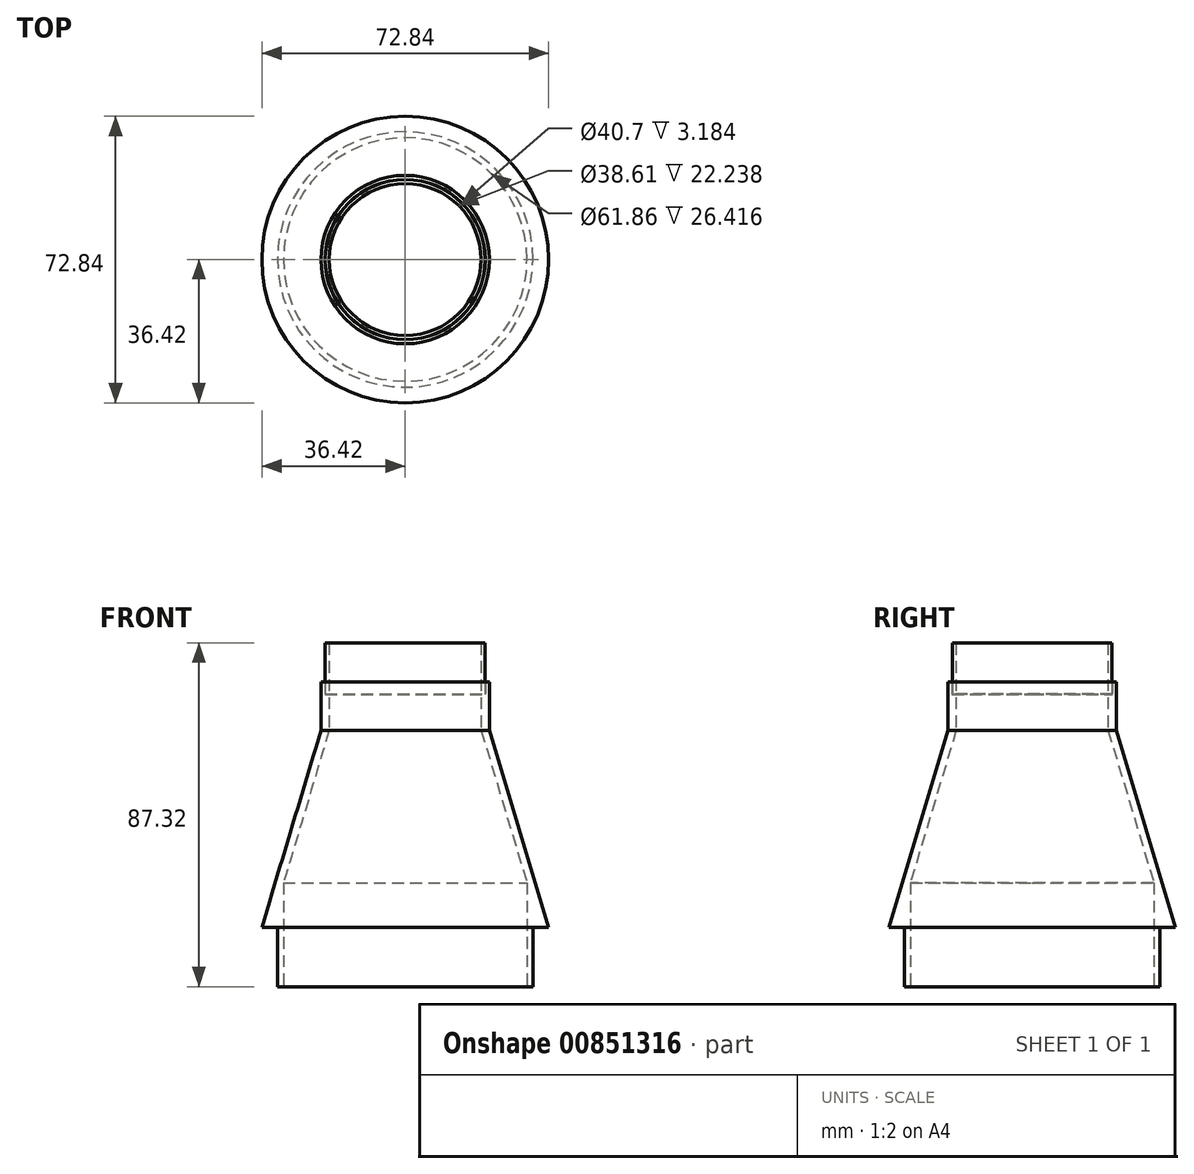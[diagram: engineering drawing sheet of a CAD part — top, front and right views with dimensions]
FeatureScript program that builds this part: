
annotation { "Feature Type Name" : "Feature", "Feature Type Description" : "" }
export const myFeature = defineFeature(function(context is Context, id is Id, definition is map)
    precondition{}
    {
        {
            var Q0;
            Q0=qCreatedBy(makeId("Front.planeOp"),FACE);
            var sketch = newSketch(context, id + "F0", { "sketchPlane" : qUnion([Q0])});
            skLineSegment(sketch, "E0", {"start": v(0, 0) * mm, "end": v(0, 50) * mm});
            skPoint(sketch, "E1", {"position": v(36.42, 0) * mm});
            skPoint(sketch, "E2", {"position": v(21.4, 50) * mm});
            skLineSegment(sketch, "E3", {"start": v(21.4, 50) * mm, "end": v(36.42, 0) * mm});
            skLineSegment(sketch, "E4", {"start": v(34.34, 0) * mm, "end": v(19.3, 50) * mm});
            skLineSegment(sketch, "E5", {"start": v(19.3, 50) * mm, "end": v(19.3, 62.38) * mm});
            skLineSegment(sketch, "E6", {"start": v(19.3, 62.38) * mm, "end": v(21.4, 62.38) * mm});
            skLineSegment(sketch, "E7", {"start": v(21.4, 62.38) * mm, "end": v(21.4, 50) * mm});
            skLineSegment(sketch, "E8.bottom", {"start": v(32.45, 0) * mm, "end": v(32.45, 0) * mm});
            skLineSegment(sketch, "E8.top", {"start": v(32.45, -15.08) * mm, "end": v(32.45, -15.08) * mm});
            skLineSegment(sketch, "E8.left", {"start": v(32.45, 0) * mm, "end": v(32.45, -15.08) * mm});
            skLineSegment(sketch, "E8.right", {"start": v(32.45, 0) * mm, "end": v(32.45, -15.08) * mm});
            skLineSegment(sketch, "E9", {"start": v(32.45, 0) * mm, "end": v(36.42, 0) * mm});
            skLineSegment(sketch, "E10", {"start": v(32.45, 0) * mm, "end": v(32.45, 6.28) * mm});
            skLineSegment(sketch, "E11.bottom", {"start": v(20.32, 59.24) * mm, "end": v(20.3, 59.24) * mm});
            skLineSegment(sketch, "E11.top", {"start": v(20.32, 72.24) * mm, "end": v(20.3, 72.24) * mm});
            skLineSegment(sketch, "E11.left", {"start": v(20.32, 59.24) * mm, "end": v(20.32, 72.24) * mm});
            skLineSegment(sketch, "E11.right", {"start": v(20.3, 59.24) * mm, "end": v(20.3, 72.24) * mm});
            skLineSegment(sketch, "E12", {"start": v(20.3, 59.24) * mm, "end": v(19.3, 56.19) * mm});
            skPoint(sketch, "E13.oppositeSnap0", {"position": v(20.35, 62.38) * mm});
            skLineSegment(sketch, "E13.bottom", {"start": v(20.32, 72.24) * mm, "end": v(20.35, 72.24) * mm});
            skLineSegment(sketch, "E13.top", {"start": v(20.32, 59.2) * mm, "end": v(20.35, 59.2) * mm});
            skLineSegment(sketch, "E13.left", {"start": v(20.32, 72.24) * mm, "end": v(20.32, 59.2) * mm});
            skLineSegment(sketch, "E13.right", {"start": v(20.35, 72.24) * mm, "end": v(20.35, 59.2) * mm});
            skLineSegment(sketch, "E14.bottom", {"start": v(19.3, 62.38) * mm, "end": v(20.35, 62.38) * mm});
            skLineSegment(sketch, "E14.top", {"start": v(19.3, 72.24) * mm, "end": v(20.35, 72.24) * mm});
            skLineSegment(sketch, "E14.left", {"start": v(19.3, 62.38) * mm, "end": v(19.3, 72.24) * mm});
            skLineSegment(sketch, "E14.right", {"start": v(20.35, 62.38) * mm, "end": v(20.35, 72.24) * mm});
            skLineSegment(sketch, "E15.bottom", {"start": v(32.45, 0) * mm, "end": v(30.93, 0) * mm});
            skLineSegment(sketch, "E15.top", {"start": v(32.45, -15.08) * mm, "end": v(30.93, -15.08) * mm});
            skLineSegment(sketch, "E15.right", {"start": v(30.93, 0) * mm, "end": v(30.93, -15.08) * mm});
            skLineSegment(sketch, "E16", {"start": v(30.93, 0) * mm, "end": v(30.93, 11.33) * mm});
            skSolve(sketch);
        }
        {
            var Q0;
            {var subQ1=sQuery(id+"F0.wireOp",EDGE,"E3");Q0=makeQuery(id+"F0.imprint","IMPRINT",FACE,{"disambiguationData":[TD([[makeQuery(id+"F0.imprint","IMPRINT",EDGE,{"derivedFrom":subQ1}),-1.0]])]});}
            var Q1;
            {var subQ3=sQuery(id+"F0.wireOp",EDGE,"E10");Q1=makeQuery(id+"F0.imprint","IMPRINT",FACE,{"disambiguationData":[TD([[makeQuery(id+"F0.imprint","IMPRINT",EDGE,{"derivedFrom":subQ3}),-1.0]])]});}
            var Q2;
            {var subQ0=sQuery(id+"F0.wireOp",EDGE,"E10");Q2=makeQuery(id+"F0.imprint","IMPRINT",FACE,{"disambiguationData":[TD([[makeQuery(id+"F0.imprint","IMPRINT",EDGE,{"derivedFrom":subQ0}),1.0]])]});}
            var Q3;
            Q3=makeQuery(id+"F0.imprint","IMPRINT",FACE,{"disambiguationData":[TD([[makeQuery(id+"F0.imprint","IMPRINT",EDGE,{"derivedFrom":sQuery(id+"F0.wireOp",EDGE,"E15.bottom")}),1.0]])]});
            var Q4;
            {var subQ5=sQuery(id+"F0.wireOp",EDGE,"E14.left");Q4=makeQuery(id+"F0.imprint","IMPRINT",FACE,{"disambiguationData":[TD([[makeQuery(id+"F0.imprint","IMPRINT",EDGE,{"derivedFrom":subQ5}),-1.0]])]});}
            var Q5;
            {var subQ3=sQuery(id+"F0.wireOp",EDGE,"E12");Q5=makeQuery(id+"F0.imprint","IMPRINT",FACE,{"disambiguationData":[TD([[makeQuery(id+"F0.imprint","IMPRINT",EDGE,{"derivedFrom":subQ3}),-1.0]])]});}
            var Q6;
            Q6=sQuery(id+"F0.wireOp",EDGE,"E0");
            revolve(context, id + "F1", {"surfaceOperationType" : NewSurfaceOperationType.NEW, "entities" : qUnion([Q0, Q1, Q2, Q3, Q4, Q5]), "axis" : qUnion([Q6]), "revolveType" : RevolveType.FULL});
        }
    });
